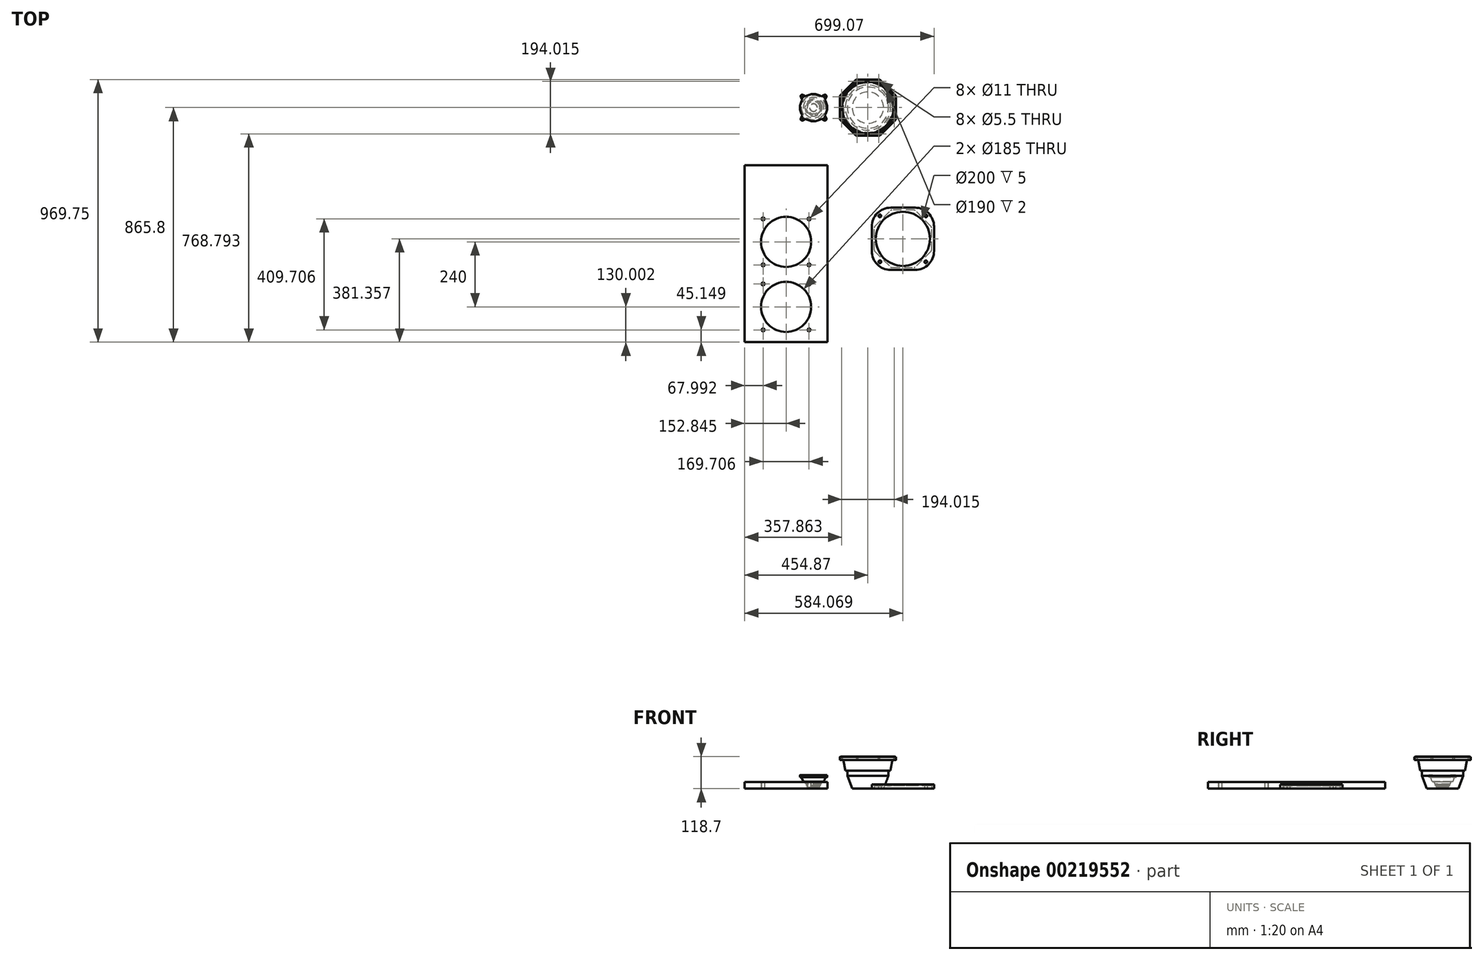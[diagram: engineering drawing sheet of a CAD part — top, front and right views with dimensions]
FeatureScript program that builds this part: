
annotation { "Feature Type Name" : "Feature", "Feature Type Description" : "" }
export const myFeature = defineFeature(function(context is Context, id is Id, definition is map)
    precondition{}
    {
        {
            var Q0;
            Q0=qCreatedBy(makeId("Front.planeOp"),FACE);
            var sketch = newSketch(context, id + "F0", { "sketchPlane" : qUnion([Q0])});
            skLineSegment(sketch, "E0", {"start": v(-51.48, 0) * mm, "end": v(-64.88, 0) * mm});
            skLineSegment(sketch, "E1", {"start": v(-64.88, 0) * mm, "end": v(-65.84, 3.7) * mm});
            skLineSegment(sketch, "E2", {"start": v(-65.84, 3.7) * mm, "end": v(-74.48, 7.04) * mm});
            skLineSegment(sketch, "E3", {"start": v(-74.48, 7.04) * mm, "end": v(-74.48, 11.7) * mm});
            skLineSegment(sketch, "E4", {"start": v(-74.48, 11.7) * mm, "end": v(-77.93, 11.7) * mm});
            skLineSegment(sketch, "E5", {"start": v(-77.93, 11.7) * mm, "end": v(-77.93, 17.5) * mm});
            skLineSegment(sketch, "E6", {"start": v(-77.93, 17.5) * mm, "end": v(-79.45, 17.5) * mm});
            skLineSegment(sketch, "E7", {"start": v(-79.45, 17.5) * mm, "end": v(-83.22, 26.26) * mm});
            skLineSegment(sketch, "E8", {"start": v(-83.22, 26.26) * mm, "end": v(-89.2, 26.26) * mm});
            skLineSegment(sketch, "E9", {"start": v(-89.2, 26.26) * mm, "end": v(-96.23, 42.6) * mm});
            skLineSegment(sketch, "E10", {"start": v(-96.23, 42.6) * mm, "end": v(-101.73, 42.6) * mm});
            skLineSegment(sketch, "E11", {"start": v(-101.73, 42.6) * mm, "end": v(-101.73, 49.8) * mm});
            skLineSegment(sketch, "E12", {"start": v(-101.73, 49.8) * mm, "end": v(-51.48, 49.8) * mm});
            skLineSegment(sketch, "E13", {"start": v(-51.48, 49.8) * mm, "end": v(-51.48, 0) * mm});
            skSolve(sketch);
        }
        {
            var Q0;
            Q0 = qSketchRegion(id + "F0", true);
            var Q1;
            Q1=sQuery(id+"F0.wireOp",EDGE,"E13");
            revolve(context, id + "F1", {"entities" : qUnion([Q0]), "axis" : qUnion([Q1]), "revolveType" : RevolveType.FULL});
        }
        {
            var Q0;
            Q0=makeQuery(id+"F1.opRevolve","SWEPT_FACE",FACE,{"disambiguationData":[OSD([sQuery(id+"F0.wireOp",EDGE,"E12")])]});
            var sketch = newSketch(context, id + "F2", { "sketchPlane" : qUnion([Q0])});
            skLineSegment(sketch, "E14", {"start": v(-51.48, 0) * mm, "end": v(-114.71, 63.23) * mm, "construction": true});
            skArc(sketch, "E15", {"start": v(-97.39, 45.9) * mm, "mid": v(-99.26, 42.03) * mm, "end": v(-98.32, 37.83) * mm});
            skLineSegment(sketch, "E16", {"start": v(-98.32, 37.83) * mm, "end": v(-92.69, 28.75) * mm});
            skArc(sketch, "E17", {"start": v(-94.88, 43.4) * mm, "mid": v(-95.76, 41.28) * mm, "end": v(-94.88, 39.16) * mm});
            skArc(sketch, "E18", {"start": v(-93.82, 38.1) * mm, "mid": v(-91.7, 37.22) * mm, "end": v(-89.58, 38.1) * mm});
            skLineSegment(sketch, "E19", {"start": v(-94.88, 39.16) * mm, "end": v(-93.82, 38.1) * mm});
            skLineSegment(sketch, "E20.MirrorCS", {"start": v(-89.3, 46.84) * mm, "end": v(-80.23, 41.21) * mm});
            skArc(sketch, "E21.MirrorCS", {"start": v(-97.39, 45.9) * mm, "mid": v(-93.51, 47.78) * mm, "end": v(-89.3, 46.84) * mm});
            skArc(sketch, "E22.MirrorCS", {"start": v(-94.88, 43.4) * mm, "mid": v(-92.76, 44.28) * mm, "end": v(-90.64, 43.4) * mm});
            skLineSegment(sketch, "E23.MirrorCS", {"start": v(-90.64, 43.4) * mm, "end": v(-89.58, 42.34) * mm});
            skArc(sketch, "E24.MirrorCS", {"start": v(-89.58, 42.34) * mm, "mid": v(-88.7, 40.22) * mm, "end": v(-89.58, 38.1) * mm});
            skLineSegment(sketch, "E25", {"start": v(-51.48, -60.21) * mm, "end": v(-51.48, 63.23) * mm, "construction": true});
            skLineSegment(sketch, "E26", {"start": v(-112.96, 0) * mm, "end": v(9.12, 0) * mm, "construction": true});
            skLineSegment(sketch, "E27.MirrorCS", {"start": v(-4.64, 37.83) * mm, "end": v(-10.27, 28.75) * mm});
            skArc(sketch, "E28.MirrorCS", {"start": v(-5.57, 45.9) * mm, "mid": v(-3.7, 42.03) * mm, "end": v(-4.64, 37.83) * mm});
            skArc(sketch, "E29.MirrorCS", {"start": v(-5.57, 45.9) * mm, "mid": v(-9.45, 47.78) * mm, "end": v(-13.65, 46.84) * mm});
            skLineSegment(sketch, "E30.MirrorCS", {"start": v(-13.65, 46.84) * mm, "end": v(-22.73, 41.21) * mm});
            skArc(sketch, "E31.MirrorCS", {"start": v(-8.08, 43.4) * mm, "mid": v(-10.2, 44.28) * mm, "end": v(-12.32, 43.4) * mm});
            skLineSegment(sketch, "E32.MirrorCS", {"start": v(-8.08, 39.16) * mm, "end": v(-9.14, 38.1) * mm});
            skArc(sketch, "E33.MirrorCS", {"start": v(-9.14, 38.1) * mm, "mid": v(-11.26, 37.22) * mm, "end": v(-13.38, 38.1) * mm});
            skArc(sketch, "E34.MirrorCS", {"start": v(-8.08, 43.4) * mm, "mid": v(-7.2, 41.28) * mm, "end": v(-8.08, 39.16) * mm});
            skLineSegment(sketch, "E35.MirrorCS", {"start": v(-12.32, 43.4) * mm, "end": v(-13.38, 42.34) * mm});
            skArc(sketch, "E36.MirrorCS", {"start": v(-13.38, 42.34) * mm, "mid": v(-14.26, 40.22) * mm, "end": v(-13.38, 38.1) * mm});
            skLineSegment(sketch, "E37.MirrorCS", {"start": v(-94.88, -39.16) * mm, "end": v(-93.82, -38.1) * mm});
            skLineSegment(sketch, "E38.MirrorCS", {"start": v(-90.64, -43.4) * mm, "end": v(-89.58, -42.34) * mm});
            skLineSegment(sketch, "E39.MirrorCS", {"start": v(-89.3, -46.84) * mm, "end": v(-80.23, -41.21) * mm});
            skArc(sketch, "E40.MirrorCS", {"start": v(-93.82, -38.1) * mm, "mid": v(-91.7, -37.22) * mm, "end": v(-89.58, -38.1) * mm});
            skArc(sketch, "E41.MirrorCS", {"start": v(-94.88, -43.4) * mm, "mid": v(-95.76, -41.28) * mm, "end": v(-94.88, -39.16) * mm});
            skLineSegment(sketch, "E42.MirrorCS", {"start": v(-98.32, -37.83) * mm, "end": v(-92.69, -28.75) * mm});
            skArc(sketch, "E43.MirrorCS", {"start": v(-97.39, -45.9) * mm, "mid": v(-99.26, -42.03) * mm, "end": v(-98.32, -37.83) * mm});
            skArc(sketch, "E44.MirrorCS", {"start": v(-97.39, -45.9) * mm, "mid": v(-93.51, -47.78) * mm, "end": v(-89.3, -46.84) * mm});
            skArc(sketch, "E45.MirrorCS", {"start": v(-94.88, -43.4) * mm, "mid": v(-92.76, -44.28) * mm, "end": v(-90.64, -43.4) * mm});
            skArc(sketch, "E46.MirrorCS", {"start": v(-89.58, -42.34) * mm, "mid": v(-88.7, -40.22) * mm, "end": v(-89.58, -38.1) * mm});
            skLineSegment(sketch, "E47.MirrorCS", {"start": v(-8.08, -39.16) * mm, "end": v(-9.14, -38.1) * mm});
            skLineSegment(sketch, "E48.MirrorCS", {"start": v(-12.32, -43.4) * mm, "end": v(-13.38, -42.34) * mm});
            skArc(sketch, "E49.MirrorCS", {"start": v(-9.14, -38.1) * mm, "mid": v(-11.26, -37.22) * mm, "end": v(-13.38, -38.1) * mm});
            skArc(sketch, "E50.MirrorCS", {"start": v(-13.38, -42.34) * mm, "mid": v(-14.26, -40.22) * mm, "end": v(-13.38, -38.1) * mm});
            skArc(sketch, "E51.MirrorCS", {"start": v(-8.08, -43.4) * mm, "mid": v(-10.2, -44.28) * mm, "end": v(-12.32, -43.4) * mm});
            skLineSegment(sketch, "E52.MirrorCS", {"start": v(-4.64, -37.83) * mm, "end": v(-10.27, -28.75) * mm});
            skArc(sketch, "E53.MirrorCS", {"start": v(-5.57, -45.9) * mm, "mid": v(-3.7, -42.03) * mm, "end": v(-4.64, -37.83) * mm});
            skArc(sketch, "E54.MirrorCS", {"start": v(-5.57, -45.9) * mm, "mid": v(-9.45, -47.78) * mm, "end": v(-13.65, -46.84) * mm});
            skLineSegment(sketch, "E55.MirrorCS", {"start": v(-13.65, -46.84) * mm, "end": v(-22.73, -41.21) * mm});
            skArc(sketch, "E56.MirrorCS", {"start": v(-8.08, -43.4) * mm, "mid": v(-7.2, -41.28) * mm, "end": v(-8.08, -39.16) * mm});
            skArc(sketch, "E57", {"start": v(-92.69, 28.75) * mm, "mid": v(-87.01, 35.53) * mm, "end": v(-80.23, 41.21) * mm});
            skArc(sketch, "E58", {"start": v(-22.73, 41.21) * mm, "mid": v(-15.95, 35.53) * mm, "end": v(-10.27, 28.75) * mm});
            skArc(sketch, "E59", {"start": v(-10.27, -28.75) * mm, "mid": v(-15.95, -35.53) * mm, "end": v(-22.73, -41.21) * mm});
            skArc(sketch, "E60", {"start": v(-80.23, -41.21) * mm, "mid": v(-87.01, -35.53) * mm, "end": v(-92.69, -28.75) * mm});
            skSolve(sketch);
        }
        {
            var Q0;
            Q0 = qSketchRegion(id + "F2", true);
            extrude(context, id + "F3", {"entities" : qUnion([Q0]), "operationType" : NewBodyOperationType.ADD, "oppositeDirection" : true, "depth" : 7.2 * mm});
        }
        {
            var Q0;
            Q0=qCreatedBy(makeId("Front.planeOp"),FACE);
            var sketch = newSketch(context, id + "F4", { "sketchPlane" : qUnion([Q0])});
            skLineSegment(sketch, "E61", {"start": v(149.18, 0) * mm, "end": v(91.28, 0) * mm});
            skLineSegment(sketch, "E62", {"start": v(91.28, 0) * mm, "end": v(73.18, 47.87) * mm});
            skLineSegment(sketch, "E63", {"start": v(73.18, 47.87) * mm, "end": v(73.18, 66.88) * mm});
            skLineSegment(sketch, "E64", {"start": v(73.18, 66.88) * mm, "end": v(66.01, 66.88) * mm});
            skLineSegment(sketch, "E65", {"start": v(66.01, 66.88) * mm, "end": v(58.68, 106) * mm});
            skLineSegment(sketch, "E66", {"start": v(58.68, 106) * mm, "end": v(149.18, 106) * mm});
            skLineSegment(sketch, "E67", {"start": v(149.18, 106) * mm, "end": v(149.18, 0) * mm});
            skSolve(sketch);
        }
        {
            var Q0;
            Q0 = qSketchRegion(id + "F4", true);
            var Q1;
            Q1=sQuery(id+"F4.wireOp",EDGE,"E67");
            revolve(context, id + "F5", {"entities" : qUnion([Q0]), "axis" : qUnion([Q1]), "revolveType" : RevolveType.FULL});
        }
        {
            var Q0;
            Q0=makeQuery(id+"F5.opRevolve","SWEPT_FACE",FACE,{"disambiguationData":[OSD([sQuery(id+"F4.wireOp",EDGE,"E66")])]});
            var sketch = newSketch(context, id + "F6", { "sketchPlane" : qUnion([Q0])});
            skLineSegment(sketch, "E68", {"start": v(45.23, 0) * mm, "end": v(45.23, -39.95) * mm});
            skLineSegment(sketch, "E69", {"start": v(47.43, -45.25) * mm, "end": v(103.93, -101.75) * mm});
            skLineSegment(sketch, "E70", {"start": v(109.23, -103.95) * mm, "end": v(149.18, -103.95) * mm});
            skLineSegment(sketch, "E71", {"start": v(282.75, 0) * mm, "end": v(40.28, 0) * mm, "construction": true});
            skLineSegment(sketch, "E72", {"start": v(149.18, 0) * mm, "end": v(149.18, -122.2) * mm, "construction": true});
            skLineSegment(sketch, "E73", {"start": v(149.18, 0) * mm, "end": v(36.96, -112.22) * mm, "construction": true});
            skLineSegment(sketch, "E74", {"start": v(45.23, -43.06) * mm, "end": v(149.18, 0) * mm, "construction": true});
            skLineSegment(sketch, "E75", {"start": v(106.12, -103.95) * mm, "end": v(149.18, 0) * mm, "construction": true});
            skCircle(sketch, "E76", {"center": v(52.17, -40.18) * mm, "radius": 2.75 * mm});
            skCircle(sketch, "E77", {"center": v(109, -97) * mm, "radius": 2.75 * mm});
            skPoint(sketch, "E78.visualSharp", {"position": v(45.23, -43.06) * mm});
            skArc(sketch, "E78.filletArc", {"start": v(45.23, -39.95) * mm, "mid": v(45.8, -42.82) * mm, "end": v(47.43, -45.25) * mm});
            skPoint(sketch, "E79.visualSharp", {"position": v(106.12, -103.95) * mm});
            skArc(sketch, "E79.filletArc", {"start": v(103.93, -101.75) * mm, "mid": v(106.36, -103.38) * mm, "end": v(109.23, -103.95) * mm});
            skArc(sketch, "E80.MirrorCS", {"start": v(194.43, -101.75) * mm, "mid": v(192, -103.38) * mm, "end": v(189.13, -103.95) * mm});
            skArc(sketch, "E81.MirrorCS", {"start": v(253.13, -39.95) * mm, "mid": v(252.56, -42.82) * mm, "end": v(250.93, -45.25) * mm});
            skCircle(sketch, "E82.MirrorC", {"center": v(189.36, -97) * mm, "radius": 2.75 * mm});
            skPoint(sketch, "E83.MirrorP", {"position": v(253.13, -43.06) * mm});
            skLineSegment(sketch, "E84.MirrorCS", {"start": v(253.13, 0) * mm, "end": v(253.13, -39.95) * mm});
            skLineSegment(sketch, "E85.MirrorCS", {"start": v(250.93, -45.25) * mm, "end": v(194.43, -101.75) * mm});
            skCircle(sketch, "E86.MirrorC", {"center": v(246.19, -40.18) * mm, "radius": 2.75 * mm});
            skLineSegment(sketch, "E87.MirrorCS", {"start": v(149.18, 0) * mm, "end": v(261.4, -112.22) * mm, "construction": true});
            skLineSegment(sketch, "E88.MirrorCS", {"start": v(192.24, -103.95) * mm, "end": v(149.18, 0) * mm, "construction": true});
            skLineSegment(sketch, "E89.MirrorCS", {"start": v(253.13, -43.06) * mm, "end": v(149.18, 0) * mm, "construction": true});
            skPoint(sketch, "E90.MirrorP", {"position": v(192.24, -103.95) * mm});
            skLineSegment(sketch, "E91.MirrorCS", {"start": v(189.13, -103.95) * mm, "end": v(149.18, -103.95) * mm});
            skArc(sketch, "E92.MirrorCS", {"start": v(194.43, 101.75) * mm, "mid": v(192, 103.38) * mm, "end": v(189.13, 103.95) * mm});
            skArc(sketch, "E93.MirrorCS", {"start": v(103.93, 101.75) * mm, "mid": v(106.36, 103.38) * mm, "end": v(109.23, 103.95) * mm});
            skArc(sketch, "E94.MirrorCS", {"start": v(45.23, 39.95) * mm, "mid": v(45.8, 42.82) * mm, "end": v(47.43, 45.25) * mm});
            skArc(sketch, "E95.MirrorCS", {"start": v(253.13, 39.95) * mm, "mid": v(252.56, 42.82) * mm, "end": v(250.93, 45.25) * mm});
            skLineSegment(sketch, "E96.MirrorCS", {"start": v(192.24, 103.95) * mm, "end": v(149.18, 0) * mm, "construction": true});
            skLineSegment(sketch, "E97.MirrorCS", {"start": v(189.13, 103.95) * mm, "end": v(149.18, 103.95) * mm});
            skCircle(sketch, "E98.MirrorC", {"center": v(109, 97) * mm, "radius": 2.75 * mm});
            skCircle(sketch, "E99.MirrorC", {"center": v(52.17, 40.18) * mm, "radius": 2.75 * mm});
            skLineSegment(sketch, "E100.MirrorCS", {"start": v(106.12, 103.95) * mm, "end": v(149.18, 0) * mm, "construction": true});
            skLineSegment(sketch, "E101.MirrorCS", {"start": v(45.23, 43.06) * mm, "end": v(149.18, 0) * mm, "construction": true});
            skLineSegment(sketch, "E102.MirrorCS", {"start": v(149.18, 0) * mm, "end": v(36.96, 112.22) * mm, "construction": true});
            skLineSegment(sketch, "E103.MirrorCS", {"start": v(149.18, 0) * mm, "end": v(149.18, 122.2) * mm, "construction": true});
            skLineSegment(sketch, "E104.MirrorCS", {"start": v(109.23, 103.95) * mm, "end": v(149.18, 103.95) * mm});
            skLineSegment(sketch, "E105.MirrorCS", {"start": v(45.23, 0) * mm, "end": v(45.23, 39.95) * mm});
            skPoint(sketch, "E106.MirrorP", {"position": v(45.23, 43.06) * mm});
            skPoint(sketch, "E107.MirrorP", {"position": v(192.24, 103.95) * mm});
            skPoint(sketch, "E108.MirrorP", {"position": v(253.13, 43.06) * mm});
            skCircle(sketch, "E109.MirrorC", {"center": v(246.19, 40.18) * mm, "radius": 2.75 * mm});
            skCircle(sketch, "E110.MirrorC", {"center": v(189.36, 97) * mm, "radius": 2.75 * mm});
            skPoint(sketch, "E111.MirrorP", {"position": v(106.12, 103.95) * mm});
            skLineSegment(sketch, "E112.MirrorCS", {"start": v(253.13, 0) * mm, "end": v(253.13, 39.95) * mm});
            skLineSegment(sketch, "E113.MirrorCS", {"start": v(253.13, 43.06) * mm, "end": v(149.18, 0) * mm, "construction": true});
            skLineSegment(sketch, "E114.MirrorCS", {"start": v(149.18, 0) * mm, "end": v(261.4, 112.22) * mm, "construction": true});
            skLineSegment(sketch, "E115.MirrorCS", {"start": v(250.93, 45.25) * mm, "end": v(194.43, 101.75) * mm});
            skLineSegment(sketch, "E116.MirrorCS", {"start": v(47.43, 45.25) * mm, "end": v(103.93, 101.75) * mm});
            skSolve(sketch);
        }
        {
            var Q0;
            Q0 = qSketchRegion(id + "F6", true);
            extrude(context, id + "F7", {"entities" : qUnion([Q0]), "operationType" : NewBodyOperationType.ADD, "depth" : 10.7 * mm});
        }
        {
            var Q0;
            Q0=makeQuery(id+"F7.opExtrude","CAP_FACE",FACE,{"disambiguationData":[OSD([sQuery(id+"F6.wireOp",EDGE,"E68"),sQuery(id+"F6.wireOp",EDGE,"E69"),sQuery(id+"F6.wireOp",EDGE,"E70"),sQuery(id+"F6.wireOp",EDGE,"E76"),sQuery(id+"F6.wireOp",EDGE,"E77"),sQuery(id+"F6.wireOp",EDGE,"E78.filletArc"),sQuery(id+"F6.wireOp",EDGE,"E79.filletArc"),sQuery(id+"F6.wireOp",EDGE,"E80.MirrorCS"),sQuery(id+"F6.wireOp",EDGE,"E81.MirrorCS"),sQuery(id+"F6.wireOp",EDGE,"E82.MirrorC"),sQuery(id+"F6.wireOp",EDGE,"E84.MirrorCS"),sQuery(id+"F6.wireOp",EDGE,"E85.MirrorCS"),sQuery(id+"F6.wireOp",EDGE,"E86.MirrorC"),sQuery(id+"F6.wireOp",EDGE,"E91.MirrorCS"),sQuery(id+"F6.wireOp",EDGE,"E92.MirrorCS"),sQuery(id+"F6.wireOp",EDGE,"E93.MirrorCS"),sQuery(id+"F6.wireOp",EDGE,"E94.MirrorCS"),sQuery(id+"F6.wireOp",EDGE,"E95.MirrorCS"),sQuery(id+"F6.wireOp",EDGE,"E97.MirrorCS"),sQuery(id+"F6.wireOp",EDGE,"E98.MirrorC"),sQuery(id+"F6.wireOp",EDGE,"E99.MirrorC"),sQuery(id+"F6.wireOp",EDGE,"E104.MirrorCS"),sQuery(id+"F6.wireOp",EDGE,"E105.MirrorCS"),sQuery(id+"F6.wireOp",EDGE,"E109.MirrorC"),sQuery(id+"F6.wireOp",EDGE,"E110.MirrorC"),sQuery(id+"F6.wireOp",EDGE,"E112.MirrorCS"),sQuery(id+"F6.wireOp",EDGE,"E115.MirrorCS"),sQuery(id+"F6.wireOp",EDGE,"E116.MirrorCS")])],"isStart":false});
            var sketch = newSketch(context, id + "F8", { "sketchPlane" : qUnion([Q0])});
            skLineSegment(sketch, "E117", {"start": v(109, -97) * mm, "end": v(189.36, 97) * mm, "construction": true});
            skCircle(sketch, "E118", {"center": v(149.18, 0) * mm, "radius": 100 * mm});
            skCircle(sketch, "E119", {"center": v(149.18, 0) * mm, "radius": 95 * mm});
            skSolve(sketch);
        }
        {
            var Q0;
            Q0 = qSketchRegion(id + "F8", true);
            extrude(context, id + "F9", {"entities" : qUnion([Q0]), "operationType" : NewBodyOperationType.ADD, "depth" : 2 * mm});
        }
        {
            var Q0;
            Q0=qCreatedBy(makeId("Top.planeOp"),FACE);
            var sketch = newSketch(context, id + "F10", { "sketchPlane" : qUnion([Q0])});
            skLineSegment(sketch, "E120.bottom", {"start": v(0, -212.17) * mm, "end": v(-305.7, -212.17) * mm});
            skLineSegment(sketch, "E120.top", {"start": v(0, -865.8) * mm, "end": v(-305.7, -865.8) * mm});
            skLineSegment(sketch, "E120.left", {"start": v(0, -212.17) * mm, "end": v(0, -865.8) * mm});
            skLineSegment(sketch, "E120.right", {"start": v(-305.7, -212.17) * mm, "end": v(-305.7, -865.8) * mm});
            skCircle(sketch, "E121", {"center": v(-152.85, -735.8) * mm, "radius": 92.5 * mm});
            skLineSegment(sketch, "E122", {"start": v(-152.85, -212.17) * mm, "end": v(-152.85, -865.8) * mm, "construction": true});
            skLineSegment(sketch, "E123", {"start": v(-152.85, -735.8) * mm, "end": v(-281, -607.64) * mm, "construction": true});
            skLineSegment(sketch, "E124", {"start": v(-152.85, -735.8) * mm, "end": v(-284.3, -735.8) * mm, "construction": true});
            skCircle(sketch, "E125", {"center": v(-237.7, -650.95) * mm, "radius": 5.5 * mm});
            skCircle(sketch, "E126.MirrorC", {"center": v(-68, -650.95) * mm, "radius": 5.5 * mm});
            skCircle(sketch, "E127.MirrorC", {"center": v(-237.7, -820.65) * mm, "radius": 5.5 * mm});
            skCircle(sketch, "E128.MirrorC", {"center": v(-68, -820.65) * mm, "radius": 5.5 * mm});
            skCircle(sketch, "E129.0.1.0", {"center": v(-152.85, -495.8) * mm, "radius": 92.5 * mm});
            skCircle(sketch, "E129.0.1.1", {"center": v(-237.7, -410.95) * mm, "radius": 5.5 * mm});
            skCircle(sketch, "E129.0.1.2", {"center": v(-237.7, -580.65) * mm, "radius": 5.5 * mm});
            skCircle(sketch, "E129.0.1.3", {"center": v(-68, -580.65) * mm, "radius": 5.5 * mm});
            skCircle(sketch, "E129.0.1.4", {"center": v(-68, -410.95) * mm, "radius": 5.5 * mm});
            skLineSegment(sketch, "E129.direction1", {"start": v(-152.85, -735.8) * mm, "end": v(-127.85, -735.8) * mm, "construction": true});
            skLineSegment(sketch, "E129.direction2", {"start": v(-152.85, -735.8) * mm, "end": v(-152.85, -495.8) * mm, "construction": true});
            skSolve(sketch);
        }
        {
            var Q0;
            Q0=qCreatedBy(makeId("Top.planeOp"),FACE);
            var sketch = newSketch(context, id + "F11", { "sketchPlane" : qUnion([Q0])});
            skLineSegment(sketch, "E130.bottom", {"start": v(233.38, -369.44) * mm, "end": v(323.38, -369.44) * mm});
            skLineSegment(sketch, "E130.top", {"start": v(233.38, -599.44) * mm, "end": v(323.38, -599.44) * mm});
            skLineSegment(sketch, "E130.left", {"start": v(163.38, -439.44) * mm, "end": v(163.38, -529.44) * mm});
            skLineSegment(sketch, "E130.right", {"start": v(393.38, -439.44) * mm, "end": v(393.38, -529.44) * mm});
            skCircle(sketch, "E131", {"center": v(278.38, -484.44) * mm, "radius": 100 * mm});
            skPoint(sketch, "E131.centerSnap0", {"position": v(163.38, -484.44) * mm});
            skPoint(sketch, "E131.centerSnap1", {"position": v(278.38, -599.44) * mm});
            skCircle(sketch, "E132", {"center": v(193.53, -399.6) * mm, "radius": 5 * mm});
            skLineSegment(sketch, "E133", {"start": v(163.38, -369.44) * mm, "end": v(393.38, -599.44) * mm, "construction": true});
            skLineSegment(sketch, "E134", {"start": v(278.38, -369.44) * mm, "end": v(278.38, -599.44) * mm, "construction": true});
            skLineSegment(sketch, "E135", {"start": v(163.38, -484.44) * mm, "end": v(393.38, -484.44) * mm, "construction": true});
            skCircle(sketch, "E136.MirrorC", {"center": v(193.53, -569.3) * mm, "radius": 5 * mm});
            skCircle(sketch, "E137.MirrorC", {"center": v(363.23, -569.3) * mm, "radius": 5 * mm});
            skCircle(sketch, "E138.MirrorC", {"center": v(363.23, -399.6) * mm, "radius": 5 * mm});
            skPoint(sketch, "E139.visualSharp", {"position": v(163.38, -369.44) * mm});
            skArc(sketch, "E139.filletArc", {"start": v(233.38, -369.44) * mm, "mid": v(183.88, -389.95) * mm, "end": v(163.38, -439.44) * mm});
            skPoint(sketch, "E140.visualSharp", {"position": v(163.38, -599.44) * mm});
            skArc(sketch, "E140.filletArc", {"start": v(163.38, -529.44) * mm, "mid": v(183.88, -578.94) * mm, "end": v(233.38, -599.44) * mm});
            skPoint(sketch, "E141.visualSharp", {"position": v(393.38, -599.44) * mm});
            skArc(sketch, "E141.filletArc", {"start": v(323.38, -599.44) * mm, "mid": v(372.88, -578.94) * mm, "end": v(393.38, -529.44) * mm});
            skPoint(sketch, "E142.visualSharp", {"position": v(393.38, -369.44) * mm});
            skArc(sketch, "E142.filletArc", {"start": v(393.38, -439.44) * mm, "mid": v(372.88, -389.95) * mm, "end": v(323.38, -369.44) * mm});
            skSolve(sketch);
        }
        {
            var Q0;
            Q0 = qSketchRegion(id + "F11", true);
            extrude(context, id + "F12", {"entities" : qUnion([Q0]), "depth" : (5 + 10.7) * mm});
        }
        {
            var Q0;
            Q0 = qSketchRegion(id + "F10", true);
            extrude(context, id + "F13", {"entities" : qUnion([Q0]), "depth" : 25 * mm});
        }
        {
            var Q0;
            Q0=qCreatedBy(makeId("Top.planeOp"),FACE);
            var sketch = newSketch(context, id + "F14", { "sketchPlane" : qUnion([Q0])});
            skLineSegment(sketch, "E143", {"start": v(193.53, -399.6) * mm, "end": v(363.23, -569.3) * mm, "construction": true});
            skLineSegment(sketch, "E144", {"start": v(363.23, -399.6) * mm, "end": v(193.53, -569.3) * mm, "construction": true});
            skLineSegment(sketch, "E145", {"start": v(278.38, -364.76) * mm, "end": v(278.38, -609.04) * mm, "construction": true});
            skPoint(sketch, "E145.startSnap0", {"position": v(278.38, -484.44) * mm});
            skLineSegment(sketch, "E146", {"start": v(155.7, -484.44) * mm, "end": v(405.55, -484.44) * mm, "construction": true});
            skCircle(sketch, "E147", {"center": v(278.38, -484.44) * mm, "radius": 100 * mm});
            skLineSegment(sketch, "E148", {"start": v(172.43, -484.44) * mm, "end": v(172.43, -525.22) * mm});
            skLineSegment(sketch, "E149", {"start": v(174.63, -530.53) * mm, "end": v(232.3, -588.2) * mm});
            skLineSegment(sketch, "E150", {"start": v(237.6, -590.4) * mm, "end": v(278.38, -590.4) * mm});
            skLineSegment(sketch, "E151.MirrorCS", {"start": v(319.16, -590.4) * mm, "end": v(278.38, -590.4) * mm});
            skLineSegment(sketch, "E152.MirrorCS", {"start": v(382.13, -530.53) * mm, "end": v(324.46, -588.2) * mm});
            skLineSegment(sketch, "E153.MirrorCS", {"start": v(384.33, -484.44) * mm, "end": v(384.33, -525.22) * mm});
            skLineSegment(sketch, "E154.MirrorCS", {"start": v(172.43, -484.44) * mm, "end": v(172.43, -443.66) * mm});
            skLineSegment(sketch, "E155.MirrorCS", {"start": v(174.63, -438.36) * mm, "end": v(232.3, -380.7) * mm});
            skLineSegment(sketch, "E156.MirrorCS", {"start": v(237.6, -378.5) * mm, "end": v(278.38, -378.5) * mm});
            skLineSegment(sketch, "E157.MirrorCS", {"start": v(319.16, -378.5) * mm, "end": v(278.38, -378.5) * mm});
            skLineSegment(sketch, "E158.MirrorCS", {"start": v(382.13, -438.36) * mm, "end": v(324.46, -380.7) * mm});
            skLineSegment(sketch, "E159.MirrorCS", {"start": v(384.33, -484.44) * mm, "end": v(384.33, -443.66) * mm});
            skPoint(sketch, "E160.visualSharp", {"position": v(172.43, -440.56) * mm});
            skArc(sketch, "E160.filletArc", {"start": v(174.63, -438.36) * mm, "mid": v(173, -440.8) * mm, "end": v(172.43, -443.66) * mm});
            skPoint(sketch, "E161.visualSharp", {"position": v(234.5, -378.5) * mm});
            skArc(sketch, "E161.filletArc", {"start": v(237.6, -378.5) * mm, "mid": v(234.73, -379.06) * mm, "end": v(232.3, -380.7) * mm});
            skPoint(sketch, "E162.visualSharp", {"position": v(322.26, -378.5) * mm});
            skArc(sketch, "E162.filletArc", {"start": v(324.46, -380.7) * mm, "mid": v(322.03, -379.06) * mm, "end": v(319.16, -378.5) * mm});
            skPoint(sketch, "E163.visualSharp", {"position": v(384.33, -440.56) * mm});
            skArc(sketch, "E163.filletArc", {"start": v(384.33, -443.66) * mm, "mid": v(383.76, -440.8) * mm, "end": v(382.13, -438.36) * mm});
            skPoint(sketch, "E164.visualSharp", {"position": v(384.33, -528.33) * mm});
            skArc(sketch, "E164.filletArc", {"start": v(382.13, -530.53) * mm, "mid": v(383.76, -528.1) * mm, "end": v(384.33, -525.22) * mm});
            skPoint(sketch, "E165.visualSharp", {"position": v(322.26, -590.4) * mm});
            skArc(sketch, "E165.filletArc", {"start": v(319.16, -590.4) * mm, "mid": v(322.03, -589.82) * mm, "end": v(324.46, -588.2) * mm});
            skPoint(sketch, "E166.visualSharp", {"position": v(234.5, -590.4) * mm});
            skArc(sketch, "E166.filletArc", {"start": v(232.3, -588.2) * mm, "mid": v(234.73, -589.82) * mm, "end": v(237.6, -590.4) * mm});
            skPoint(sketch, "E167.visualSharp", {"position": v(172.43, -528.33) * mm});
            skArc(sketch, "E167.filletArc", {"start": v(172.43, -525.22) * mm, "mid": v(173, -528.1) * mm, "end": v(174.63, -530.53) * mm});
            skSolve(sketch);
        }
        {
            var Q0;
            Q0 = qSketchRegion(id + "F14", true);
            extrude(context, id + "F15", {"entities" : qUnion([Q0]), "operationType" : NewBodyOperationType.REMOVE, "depth" : 10.7 * mm});
        }
    });
